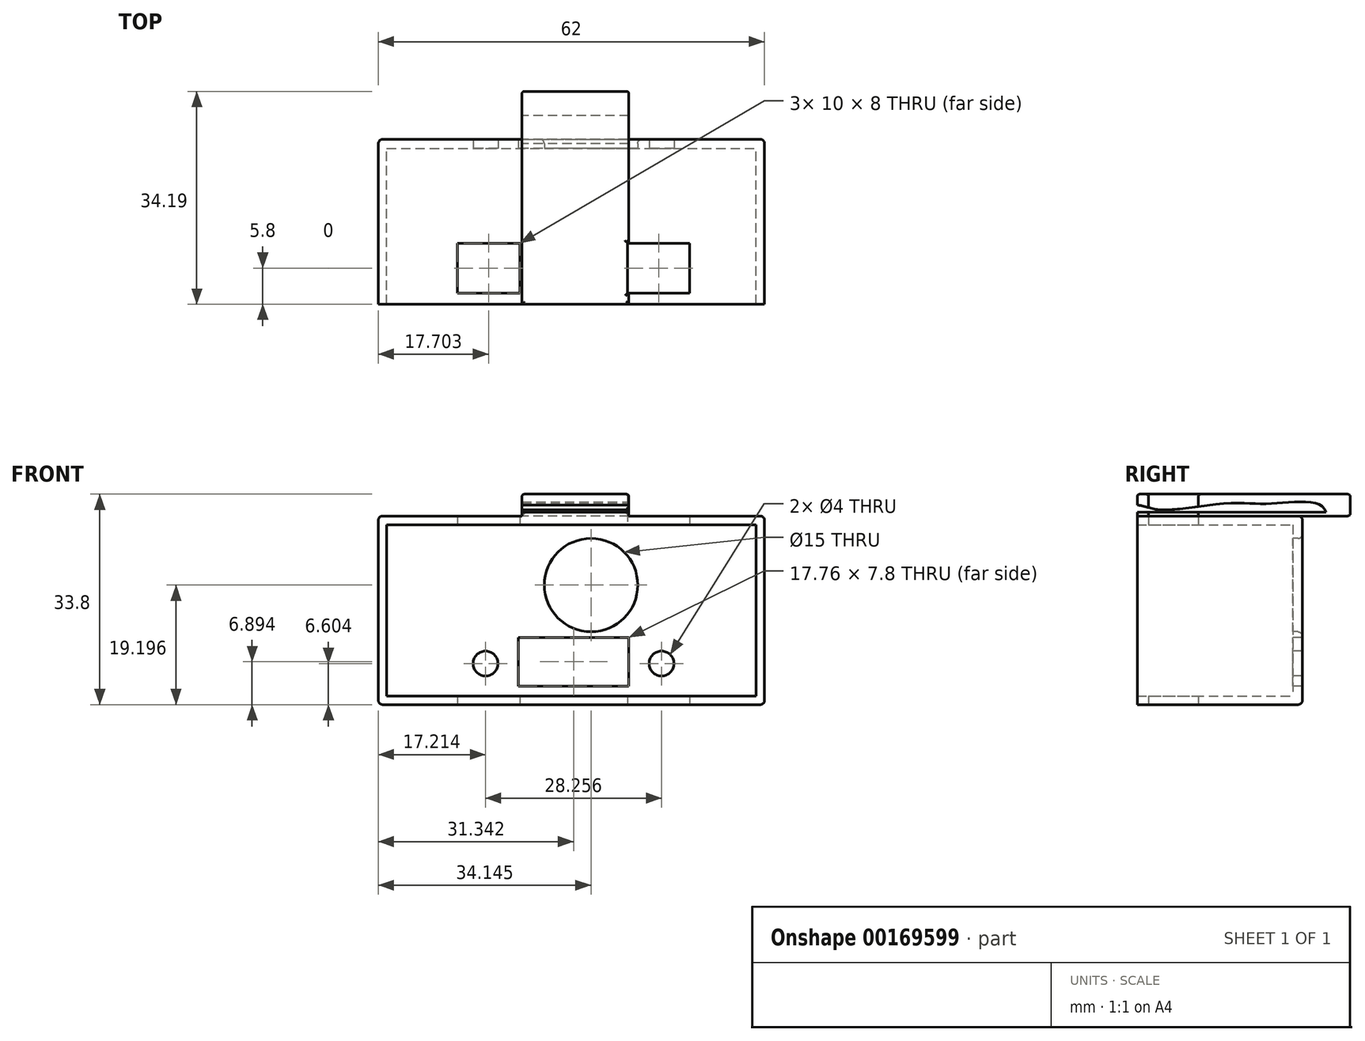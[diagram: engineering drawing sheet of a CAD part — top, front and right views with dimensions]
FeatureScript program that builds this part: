
annotation { "Feature Type Name" : "Feature", "Feature Type Description" : "" }
export const myFeature = defineFeature(function(context is Context, id is Id, definition is map)
    precondition{}
    {
        {
            var Q0;
            Q0=qCreatedBy(makeId("Front.planeOp"),FACE);
            var sketch = newSketch(context, id + "F0", { "sketchPlane" : qUnion([Q0])});
            skLineSegment(sketch, "E0.bottom", {"start": v(-38.87, 27.5) * mm, "end": v(20.43, 27.5) * mm});
            skLineSegment(sketch, "E0.top", {"start": v(-38.87, 0) * mm, "end": v(20.43, 0) * mm});
            skLineSegment(sketch, "E0.left", {"start": v(-38.87, 27.5) * mm, "end": v(-38.87, 0) * mm});
            skLineSegment(sketch, "E0.right", {"start": v(20.43, 27.5) * mm, "end": v(20.43, 0) * mm});
            skSolve(sketch);
        }
        {
            var Q0;
            Q0=qCreatedBy(makeId("Front.planeOp"),FACE);
            var sketch = newSketch(context, id + "F1", { "sketchPlane" : qUnion([Q0])});
            skLineSegment(sketch, "E1.bottom", {"start": v(-40.22, 28.95) * mm, "end": v(21.78, 28.95) * mm});
            skLineSegment(sketch, "E1.top", {"start": v(-40.22, -1.35) * mm, "end": v(21.78, -1.35) * mm});
            skLineSegment(sketch, "E1.left", {"start": v(-40.22, 28.95) * mm, "end": v(-40.22, -1.35) * mm});
            skLineSegment(sketch, "E1.right", {"start": v(21.78, 28.95) * mm, "end": v(21.78, -1.35) * mm});
            skSolve(sketch);
        }
        {
            var Q0;
            Q0=makeQuery(id+"F1.imprint","IMPRINT",FACE,{"disambiguationData":[TD([[makeQuery(id+"F1.imprint","IMPRINT",EDGE,{"derivedFrom":sQuery(id+"F1.wireOp",EDGE,"E1.bottom")}),-1.0]])]});
            extrude(context, id + "F2", {"entities" : qUnion([Q0]), "depth" : 25 * mm, "hasSecondDirection" : true, "secondDirectionOppositeDirection" : true, "secondDirectionDepth" : 1.5 * mm});
        }
        {
            var Q0;
            Q0 = qSketchRegion(id + "F0", true);
            extrude(context, id + "F3", {"entities" : qUnion([Q0]), "operationType" : NewBodyOperationType.REMOVE, "depth" : 25 * mm});
        }
        {
            var Q0;
            Q0=makeQuery(id+"F0.imprint","IMPRINT",FACE,{"disambiguationData":[TD([[makeQuery(id+"F0.imprint","IMPRINT",EDGE,{"derivedFrom":sQuery(id+"F0.wireOp",EDGE,"E0.bottom")}),-1.0]])]});
            var sketch = newSketch(context, id + "F4", { "sketchPlane" : qUnion([Q0])});
            skCircle(sketch, "E2", {"center": v(-6.08, 17.85) * mm, "radius": 7.5 * mm});
            skSolve(sketch);
        }
        {
            var Q0;
            Q0 = qSketchRegion(id + "F4", true);
            extrude(context, id + "F5", {"entities" : qUnion([Q0]), "operationType" : NewBodyOperationType.REMOVE, "oppositeDirection" : true, "depth" : 5 * mm});
        }
        {
            var Q0;
            Q0=makeQuery(id+"F2.opExtrude","CAP_FACE",FACE,{"disambiguationData":[OSD([sQuery(id+"F1.wireOp",EDGE,"E1.bottom"),sQuery(id+"F1.wireOp",EDGE,"E1.top"),sQuery(id+"F1.wireOp",EDGE,"E1.left"),sQuery(id+"F1.wireOp",EDGE,"E1.right")])],"isStart":true});
            var Q1;
            Q1=makeQuery(id+"F2.opExtrude","SWEPT_EDGE",EDGE,{"disambiguationData":[OSD([sQuery(id+"F1.wireOp",EDGE,"E1.top"),sQuery(id+"F1.wireOp",EDGE,"E1.left")])]});
            var Q2;
            Q2=makeQuery(id+"F2.opExtrude","SWEPT_EDGE",EDGE,{"disambiguationData":[OSD([sQuery(id+"F1.wireOp",EDGE,"E1.top"),sQuery(id+"F1.wireOp",EDGE,"E1.right")])]});
            var Q3;
            Q3=makeQuery(id+"F2.opExtrude","SWEPT_EDGE",EDGE,{"disambiguationData":[OSD([sQuery(id+"F1.wireOp",EDGE,"E1.bottom"),sQuery(id+"F1.wireOp",EDGE,"E1.left")])]});
            var Q4;
            Q4=makeQuery(id+"F2.opExtrude","SWEPT_EDGE",EDGE,{"disambiguationData":[OSD([sQuery(id+"F1.wireOp",EDGE,"E1.bottom"),sQuery(id+"F1.wireOp",EDGE,"E1.right")])]});
            fillet(context, id + "F6", {"entities" : qUnion([Q0, Q1, Q2, Q3, Q4]), "radius" : 0.7 * mm, "tangentPropagation" : true, "allowEdgeOverflow" : false});
        }
        {
            var Q0;
            Q0=qCreatedBy(makeId("Top.planeOp"),FACE);
            var sketch = newSketch(context, id + "F7", { "sketchPlane" : qUnion([Q0])});
            skLineSegment(sketch, "E3.bottom", {"start": v(-27.52, -15.2) * mm, "end": v(-17.52, -15.2) * mm});
            skLineSegment(sketch, "E3.top", {"start": v(-27.52, -23.2) * mm, "end": v(-17.52, -23.2) * mm});
            skLineSegment(sketch, "E3.left", {"start": v(-27.52, -15.2) * mm, "end": v(-27.52, -23.2) * mm});
            skLineSegment(sketch, "E3.right", {"start": v(-17.52, -15.2) * mm, "end": v(-17.52, -23.2) * mm});
            skSolve(sketch);
        }
        {
            var Q0;
            Q0 = qSketchRegion(id + "F7", true);
            extrude(context, id + "F8", {"entities" : qUnion([Q0]), "operationType" : NewBodyOperationType.REMOVE, "depth" : 45 * mm, "hasSecondDirection" : true, "secondDirectionOppositeDirection" : true, "secondDirectionDepth" : 5 * mm});
        }
        {
            var Q0;
            Q0=qCreatedBy(makeId("Top.planeOp"),FACE);
            var sketch = newSketch(context, id + "F9", { "sketchPlane" : qUnion([Q0])});
            skLineSegment(sketch, "E4.bottom", {"start": v(-0.22, -15.2) * mm, "end": v(9.78, -15.2) * mm});
            skLineSegment(sketch, "E4.top", {"start": v(-0.22, -23.2) * mm, "end": v(9.78, -23.2) * mm});
            skLineSegment(sketch, "E4.left", {"start": v(-0.22, -15.2) * mm, "end": v(-0.22, -23.2) * mm});
            skLineSegment(sketch, "E4.right", {"start": v(9.78, -15.2) * mm, "end": v(9.78, -23.2) * mm});
            skSolve(sketch);
        }
        {
            var Q0;
            Q0 = qSketchRegion(id + "F9", true);
            extrude(context, id + "F10", {"entities" : qUnion([Q0]), "operationType" : NewBodyOperationType.REMOVE, "depth" : 45 * mm, "hasSecondDirection" : true, "secondDirectionOppositeDirection" : true, "secondDirectionDepth" : 5 * mm});
        }
        {
            var Q0;
            Q0=makeQuery(id+"F2.opExtrude","SWEPT_FACE",FACE,{"disambiguationData":[OSD([sQuery(id+"F1.wireOp",EDGE,"E1.bottom")])]});
            var sketch = newSketch(context, id + "F11", { "sketchPlane" : qUnion([Q0])});
            skLineSegment(sketch, "E5.bottom", {"start": v(-17.16, -25) * mm, "end": v(0, -25) * mm});
            skLineSegment(sketch, "E5.top", {"start": v(-17.16, 9.19) * mm, "end": v(0, 9.19) * mm});
            skLineSegment(sketch, "E5.left", {"start": v(-17.16, -25) * mm, "end": v(-17.16, 9.19) * mm});
            skLineSegment(sketch, "E5.right", {"start": v(0, -25) * mm, "end": v(0, 9.19) * mm});
            skSolve(sketch);
        }
        {
            var Q0;
            {var subQ0=sQuery(id+"F11.wireOp",EDGE,"E5.top");Q0=makeQuery(id+"F11.imprint","IMPRINT",FACE,{"disambiguationData":[TD([[makeQuery(id+"F11.imprint","IMPRINT",EDGE,{"derivedFrom":subQ0}),-1.0]])]});}
            var Q1;
            {var subQ0=sQuery(id+"F11.wireOp",EDGE,"E5.bottom");Q1=makeQuery(id+"F11.imprint","IMPRINT",FACE,{"disambiguationData":[TD([[makeQuery(id+"F11.imprint","IMPRINT",EDGE,{"derivedFrom":subQ0}),1.0]])]});}
            extrude(context, id + "F12", {"entities" : qUnion([Q0, Q1]), "operationType" : NewBodyOperationType.ADD, "depth" : 3.5 * mm});
        }
        {
            var Q0;
            Q0=makeQuery(id+"F12.opExtrude","SWEPT_FACE",FACE,{"disambiguationData":[OSD([sQuery(id+"F11.wireOp",EDGE,"E5.left")])]});
            var sketch = newSketch(context, id + "F13", { "sketchPlane" : qUnion([Q0])});
            skLineSegment(sketch, "E6", {"start": v(25, 30.7) * mm, "end": v(25, 29.54) * mm});
            skLineSegment(sketch, "E7", {"start": v(25, 29.54) * mm, "end": v(-5.32, 29.54) * mm});
            skFitSpline(sketch, "E8", {"points": [v(-5.32, 29.54) * mm, v(-3.98, 30.9) * mm, v(0, 31.19) * mm, v(4.87, 30.9) * mm, v(10.02, 31) * mm, v(19.73, 29.95) * mm, v(22.75, 30.17) * mm, v(25, 30.7) * mm], "startDerivative": vector(9.25, 20.1) * mm, "endDerivative": vector(20.04, 1.61) * mm});
            skSolve(sketch);
        }
        {
            var Q0;
            Q0=makeQuery(id+"F13.imprint","IMPRINT",FACE,{"disambiguationData":[TD([[makeQuery(id+"F13.imprint","IMPRINT",EDGE,{"derivedFrom":sQuery(id+"F13.wireOp",EDGE,"E6")}),-1.0]])]});
            extrude(context, id + "F14", {"entities" : qUnion([Q0]), "operationType" : NewBodyOperationType.REMOVE, "oppositeDirection" : true, "depth" : 25 * mm});
        }
        {
            var Q0;
            Q0=makeQuery(id+"F0.imprint","IMPRINT",FACE,{"disambiguationData":[TD([[makeQuery(id+"F0.imprint","IMPRINT",EDGE,{"derivedFrom":sQuery(id+"F0.wireOp",EDGE,"E0.bottom")}),-1.0]])]});
            var sketch = newSketch(context, id + "F15", { "sketchPlane" : qUnion([Q0])});
            skCircle(sketch, "E9", {"center": v(-23, 5.25) * mm, "radius": 2 * mm});
            skCircle(sketch, "E10", {"center": v(5.25, 5.25) * mm, "radius": 2 * mm});
            skLineSegment(sketch, "E11", {"start": v(-17.76, 1.64) * mm, "end": v(-17.76, 9.44) * mm});
            skLineSegment(sketch, "E12", {"start": v(3, 9.44) * mm, "end": v(3, 1.64) * mm, "construction": true});
            skLineSegment(sketch, "E13", {"start": v(0, 1.64) * mm, "end": v(0, 9.44) * mm});
            skLineSegment(sketch, "E14", {"start": v(0, 1.64) * mm, "end": v(-17.76, 1.64) * mm});
            skLineSegment(sketch, "E15", {"start": v(0, 9.44) * mm, "end": v(-17.76, 9.44) * mm});
            skSolve(sketch);
        }
        {
            var Q0;
            Q0 = qSketchRegion(id + "F15", true);
            extrude(context, id + "F16", {"entities" : qUnion([Q0]), "operationType" : NewBodyOperationType.REMOVE, "oppositeDirection" : true, "depth" : 5 * mm});
        }
        {
            var Q0;
            Q0=makeQuery(id+"F12.opExtrude","CAP_FACE",FACE,{"disambiguationData":[OSD([sQuery(id+"F1.wireOp",EDGE,"E1.bottom"),sQuery(id+"F9.wireOp",EDGE,"E4.bottom"),sQuery(id+"F9.wireOp",EDGE,"E4.top"),sQuery(id+"F9.wireOp",EDGE,"E4.left"),sQuery(id+"F11.wireOp",EDGE,"E5.bottom"),sQuery(id+"F11.wireOp",EDGE,"E5.top"),sQuery(id+"F11.wireOp",EDGE,"E5.left"),sQuery(id+"F11.wireOp",EDGE,"E5.right")])],"isStart":false});
            var Q1;
            Q1=makeQuery(id+"F12.opExtrude","CAP_EDGE",EDGE,{"disambiguationData":[OSD([sQuery(id+"F11.wireOp",EDGE,"E5.top")])],"isStart":true});
            var Q2;
            Q2=makeQuery(id+"F12.opExtrude","SWEPT_EDGE",EDGE,{"disambiguationData":[OSD([sQuery(id+"F11.wireOp",EDGE,"E5.top"),sQuery(id+"F11.wireOp",EDGE,"E5.right")])]});
            var Q3;
            Q3=makeQuery(id+"F12.opExtrude","SWEPT_EDGE",EDGE,{"disambiguationData":[OSD([sQuery(id+"F11.wireOp",EDGE,"E5.top"),sQuery(id+"F11.wireOp",EDGE,"E5.left")])]});
            fillet(context, id + "F17", {"entities" : qUnion([Q0, Q1, Q2, Q3]), "radius" : 0.4 * mm, "tangentPropagation" : true, "allowEdgeOverflow" : false});
        }
    });
